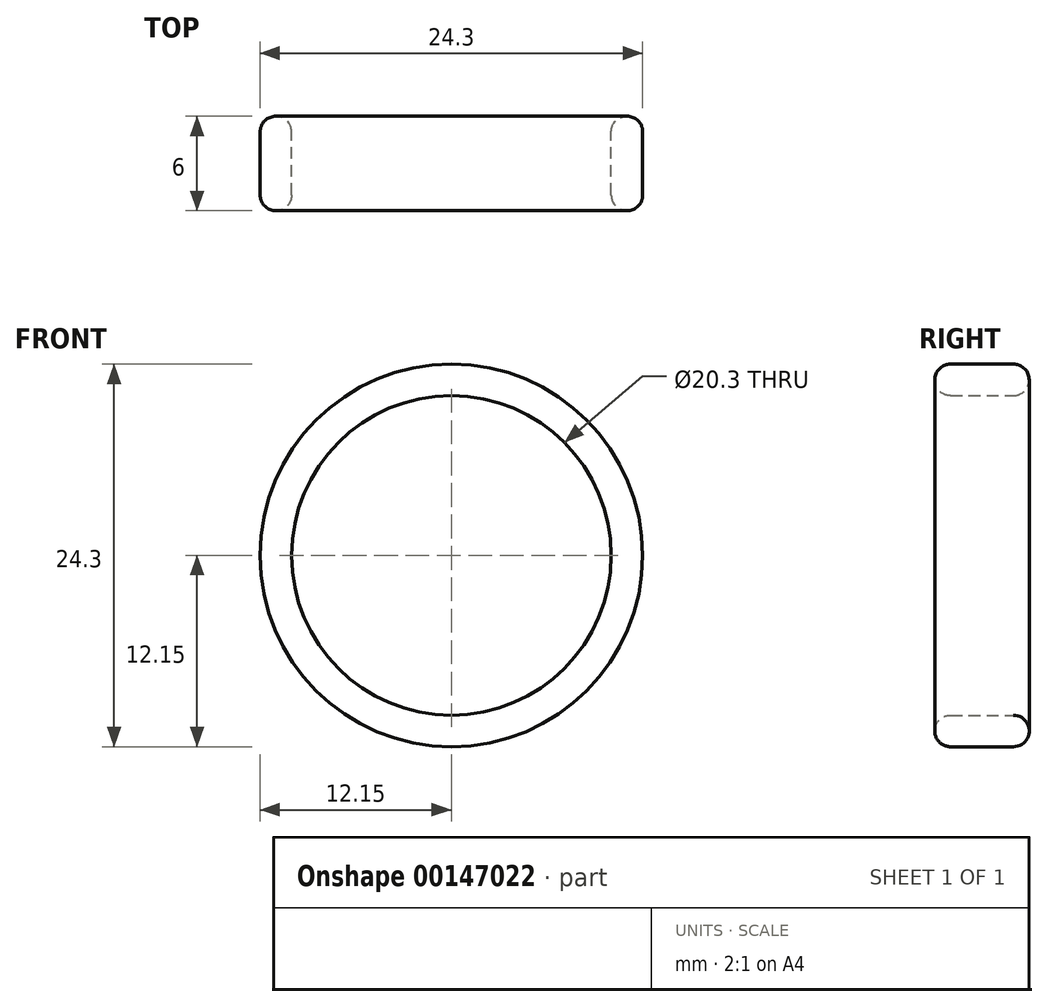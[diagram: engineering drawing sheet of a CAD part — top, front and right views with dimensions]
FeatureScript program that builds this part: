
annotation { "Feature Type Name" : "Feature", "Feature Type Description" : "" }
export const myFeature = defineFeature(function(context is Context, id is Id, definition is map)
    precondition{}
    {
        {
            var Q0;
            Q0=qCreatedBy(makeId("Front.planeOp"),FACE);
            var sketch = newSketch(context, id + "F0", { "sketchPlane" : qUnion([Q0])});
            skCircle(sketch, "E0", {"center": v(0, 0) * mm, "radius": 10.15 * mm});
            skCircle(sketch, "E1", {"center": v(0, 0) * mm, "radius": 12.15 * mm});
            skSolve(sketch);
        }
        {
            var Q0;
            Q0=makeQuery(id+"F0.imprint","IMPRINT",FACE,{"disambiguationData":[TD([[makeQuery(id+"F0.imprint","IMPRINT",EDGE,{"derivedFrom":sQuery(id+"F0.wireOp",EDGE,"E0")}),-1.0]])]});
            extrude(context, id + "F1", {"entities" : qUnion([Q0]), "depth" : 6 * mm, "offsetDistance" : 25 * mm});
        }
        {
            var Q0;
            Q0=makeQuery(id+"F1.opExtrude","CAP_EDGE",EDGE,{"disambiguationData":[OSD([sQuery(id+"F0.wireOp",EDGE,"E0")])],"isStart":false});
            var Q1;
            Q1=makeQuery(id+"F1.opExtrude","CAP_EDGE",EDGE,{"disambiguationData":[OSD([sQuery(id+"F0.wireOp",EDGE,"E0")])],"isStart":true});
            fillet(context, id + "F2", {"entities" : qUnion([Q0, Q1]), "radius" : 1 * mm, "tangentPropagation" : true, "allowEdgeOverflow" : false});
        }
        {
            var Q0;
            Q0=makeQuery(id+"F1.opExtrude","CAP_EDGE",EDGE,{"disambiguationData":[OSD([sQuery(id+"F0.wireOp",EDGE,"E1")])],"isStart":true});
            var Q1;
            Q1=makeQuery(id+"F1.opExtrude","CAP_EDGE",EDGE,{"disambiguationData":[OSD([sQuery(id+"F0.wireOp",EDGE,"E1")])],"isStart":false});
            fillet(context, id + "F3", {"entities" : qUnion([Q0, Q1]), "radius" : 1 * mm, "tangentPropagation" : true, "allowEdgeOverflow" : false});
        }
    });
